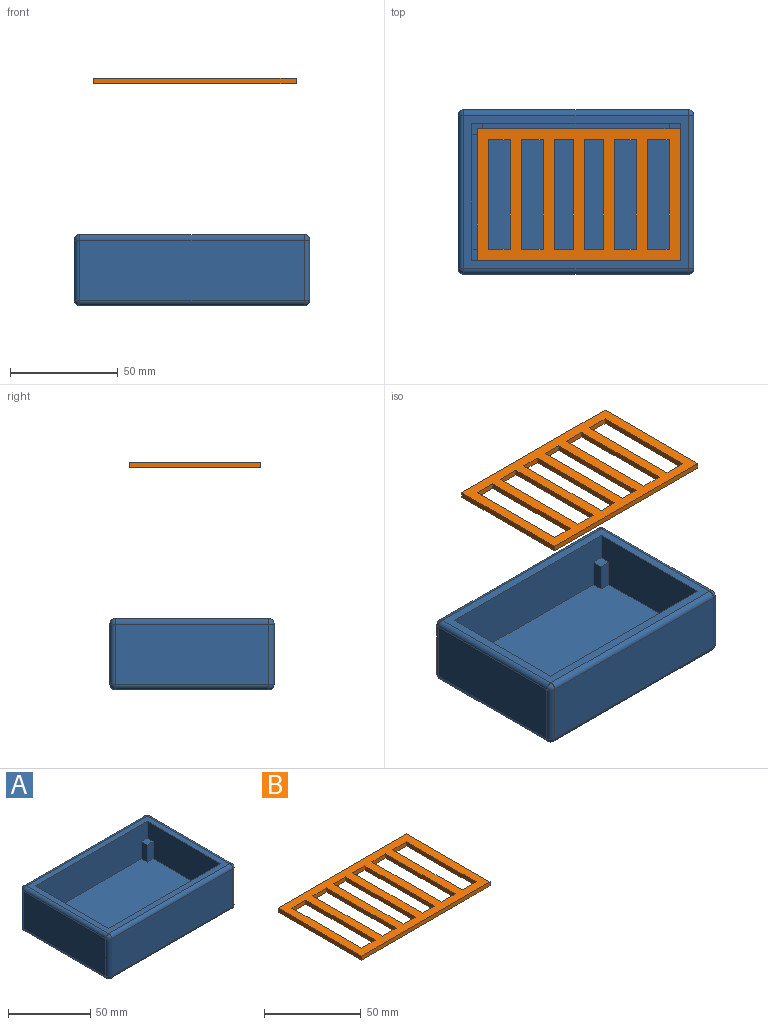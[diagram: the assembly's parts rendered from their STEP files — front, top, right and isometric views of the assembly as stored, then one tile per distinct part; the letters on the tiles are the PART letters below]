
ASSEMBLY  parts=2 mates=1
PART A: 43 faces, bbox 109.2x76.2x33 mm
  f0: plane 71.12x27.94mm, normal (1,0,0), area 1987.1mm2, adj f11,f15,f16,f17
  f1: plane 104.14x27.94mm, normal (0,1,0), area 2909.7mm2, adj f14,f15,f24,f25
  f2: plane 71.12x27.94mm, normal (-1,0,0), area 1987.1mm2, adj f19,f24,f27,f30
  f3: plane 104.14x27.94mm, normal (0,-1,0), area 2909.7mm2, adj f17,f18,f26,f27
  f4: plane 104.14x71.12mm, normal (0,0,-1), area 7406.4mm2, adj f11,f14,f18,f19
  f5: plane 63.5x25.4mm, normal (1,0,0), area 1483.9mm2, adj f6,f8,f9,f10,f32,f33,f34,f36
  f6: plane 96.52x25.4mm, normal (0,-1,0), area 2322.6mm2, adj f5,f7,f9,f10,f35,f36,f37,f39
  f7: plane 63.5x25.4mm, normal (-1,0,0), area 1483.9mm2, adj f6,f8,f9,f10,f38,f39,f40,f42
  f8: plane 96.52x25.4mm, normal (0,1,0), area 2322.6mm2, adj f5,f7,f9,f10,f31,f33,f41,f42
  f9: plane 104.14x71.12mm, normal (0,0,1), area 1277.4mm2, adj f5,f6,f7,f8,f16,f25,f26,f30
  f10: plane 96.52x63.5mm, normal (0,0,1), area 6025.8mm2, adj f5,f6,f7,f8,f31,f32,f34,f35
  f11: cylinder r=2.54mm len=71.12mm, axis (0,1,0), area 283.8mm2, adj f0,f4,f12,f13
  f12: sphere r=2.54mm, area 10.1mm2, adj f11,f14,f15
  f13: sphere r=2.54mm, area 10.1mm2, adj f11,f17,f18
  f14: cylinder r=2.54mm len=104.14mm, axis (-1,0,0), area 415.5mm2, adj f1,f4,f12,f20
  f15: cylinder r=2.54mm len=27.94mm, axis (0,0,1), area 111.5mm2, adj f0,f1,f12,f21
  f16: cylinder r=2.54mm len=71.12mm, axis (0,-1,0), area 283.8mm2, adj f0,f9,f21,f22
  f17: cylinder r=2.54mm len=27.94mm, axis (0,0,-1), area 111.5mm2, adj f0,f3,f13,f22
  f18: cylinder r=2.54mm len=104.14mm, axis (1,0,0), area 415.5mm2, adj f3,f4,f13,f23
  f19: cylinder r=2.54mm len=71.12mm, axis (0,-1,0), area 283.8mm2, adj f2,f4,f20,f23
  f20: sphere r=2.54mm, area 10.1mm2, adj f14,f19,f24
  f21: sphere r=2.54mm, area 10.1mm2, adj f15,f16,f25
  f22: sphere r=2.54mm, area 10.1mm2, adj f16,f17,f26
  f23: sphere r=2.54mm, area 10.1mm2, adj f18,f19,f27
  f24: cylinder r=2.54mm len=27.94mm, axis (0,0,-1), area 111.5mm2, adj f1,f2,f20,f28
  f25: cylinder r=2.54mm len=104.14mm, axis (1,0,0), area 415.5mm2, adj f1,f9,f21,f28
  f26: cylinder r=2.54mm len=104.14mm, axis (-1,0,0), area 415.5mm2, adj f3,f9,f22,f29
  f27: cylinder r=2.54mm len=27.94mm, axis (0,0,1), area 111.5mm2, adj f2,f3,f23,f29
  f28: sphere r=2.54mm, area 10.1mm2, adj f24,f25,f30
  f29: sphere r=2.54mm, area 10.1mm2, adj f26,f27,f30
  f30: cylinder r=2.54mm len=71.12mm, axis (0,1,0), area 283.8mm2, adj f2,f9,f28,f29
  f31: plane 12.7x5.08mm, normal (1,0,0), area 64.5mm2, adj f8,f10,f32,f33
  f32: plane 12.7x5.08mm, normal (0,1,0), area 64.5mm2, adj f5,f10,f31,f33
  f33: plane 5.08x5.08mm, normal (0,0,1), area 25.8mm2, adj f5,f8,f31,f32
  f34: plane 12.7x5.08mm, normal (0,-1,0), area 64.5mm2, adj f5,f10,f35,f36
  f35: plane 12.7x5.08mm, normal (1,0,0), area 64.5mm2, adj f6,f10,f34,f36
  f36: plane 5.08x5.08mm, normal (0,0,1), area 25.8mm2, adj f5,f6,f34,f35
  f37: plane 12.7x5.08mm, normal (-1,0,0), area 64.5mm2, adj f6,f10,f38,f39
  f38: plane 12.7x5.08mm, normal (0,-1,0), area 64.5mm2, adj f7,f10,f37,f39
  f39: plane 5.08x5.08mm, normal (0,0,1), area 25.8mm2, adj f6,f7,f37,f38
  f40: plane 12.7x5.08mm, normal (0,1,0), area 64.5mm2, adj f7,f10,f41,f42
  f41: plane 12.7x5.08mm, normal (-1,0,0), area 64.5mm2, adj f8,f10,f40,f42
  f42: plane 5.08x5.08mm, normal (0,0,1), area 25.8mm2, adj f7,f8,f40,f41
PART B: 30 faces, bbox 94x61x2.5 mm
  f0: plane 10.16x2.54mm, normal (0,-1,0), area 25.8mm2, adj f1,f27,f28,f29
  f1: plane 50.8x2.54mm, normal (-1,0,0), area 129mm2, adj f0,f2,f28,f29
  f2: plane 10.16x2.54mm, normal (0,1,0), area 25.8mm2, adj f1,f27,f28,f29
  f3: plane 8.89x2.54mm, normal (0,-1,0), area 22.6mm2, adj f4,f21,f28,f29
  f4: plane 50.8x2.54mm, normal (-1,0,0), area 129mm2, adj f3,f5,f28,f29
  f5: plane 8.89x2.54mm, normal (0,1,0), area 22.6mm2, adj f4,f21,f28,f29
  f6: plane 10.16x2.54mm, normal (0,-1,0), area 25.8mm2, adj f7,f22,f28,f29
  f7: plane 50.8x2.54mm, normal (-1,0,0), area 129mm2, adj f6,f8,f28,f29
  f8: plane 10.16x2.54mm, normal (0,1,0), area 25.8mm2, adj f7,f22,f28,f29
  f9: plane 93.98x2.54mm, normal (0,-1,0), area 238.7mm2, adj f10,f23,f28,f29
  f10: plane 60.96x2.54mm, normal (1,0,0), area 154.8mm2, adj f9,f11,f28,f29
  f11: plane 93.98x2.54mm, normal (0,1,0), area 238.7mm2, adj f10,f23,f28,f29
  f12: plane 50.8x2.54mm, normal (-1,0,0), area 129mm2, adj f13,f24,f28,f29
  f13: plane 10.16x2.54mm, normal (0,1,0), area 25.8mm2, adj f12,f14,f28,f29
  f14: plane 50.8x2.54mm, normal (1,0,0), area 129mm2, adj f13,f24,f28,f29
  f15: plane 50.8x2.54mm, normal (-1,0,0), area 129mm2, adj f16,f25,f28,f29
  f16: plane 8.89x2.54mm, normal (0,1,0), area 22.6mm2, adj f15,f17,f28,f29
  f17: plane 50.8x2.54mm, normal (1,0,0), area 129mm2, adj f16,f25,f28,f29
  f18: plane 50.8x2.54mm, normal (-1,0,0), area 129mm2, adj f19,f26,f28,f29
  f19: plane 10.16x2.54mm, normal (0,1,0), area 25.8mm2, adj f18,f20,f28,f29
  f20: plane 50.8x2.54mm, normal (1,0,0), area 129mm2, adj f19,f26,f28,f29
  f21: plane 50.8x2.54mm, normal (1,0,0), area 129mm2, adj f3,f5,f28,f29
  f22: plane 50.8x2.54mm, normal (1,0,0), area 129mm2, adj f6,f8,f28,f29
  f23: plane 60.96x2.54mm, normal (-1,0,0), area 154.8mm2, adj f9,f11,f28,f29
  f24: plane 10.16x2.54mm, normal (0,-1,0), area 25.8mm2, adj f12,f14,f28,f29
  f25: plane 8.89x2.54mm, normal (0,-1,0), area 22.6mm2, adj f15,f17,f28,f29
  f26: plane 10.16x2.54mm, normal (0,-1,0), area 25.8mm2, adj f18,f20,f28,f29
  f27: plane 50.8x2.54mm, normal (1,0,0), area 129mm2, adj f0,f2,f28,f29
  f28: plane 93.98x60.96mm, normal (0,0,1), area 2761.3mm2, adj f0,f1,f2,f3,f4,f5,f6,f7
  f29: plane 93.98x60.96mm, normal (0,0,-1), area 2761.3mm2, adj f0,f1,f2,f3,f4,f5,f6,f7
PLACE A t=(-37.83,104.47,0)mm
PLACE B t=(-36.56,103.2,102.95)mm
MATE slider B.f29 <-> A.f42  axis (0,0,-1) through (10.43,72.72,102.95)mm
